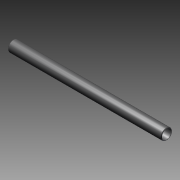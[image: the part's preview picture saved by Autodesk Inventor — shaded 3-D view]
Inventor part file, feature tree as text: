
AUTODESK INVENTOR PART (.ipt)
format: ipt  version: 2011 SP1 (Build 150282100, 282)  size: 112,128 bytes
history: native  units: in
note: dims shown in document units (in); Inventor stores cm internally (conversion verified against a paired STEP export)
features: other x42, revolve x1, sketch x1
ambient origin geometry x8: Origin, YZ Plane, XZ Plane, XY Plane, X Axis, Y Axis, Z Axis, Center Point
bodies: Solid1 (feature_tree)
feature tree (44):
  revolve  "Revolution1"  [1 undecoded]
  other  "cp1_XY"
  other  "cp1_YZ"
  other  "cp1_ZX"
  other  "cp1_X"
  other  "cp1_Y"
  other  "cp1_Z"
  other  "cp1_Center"
  other  "cp2_XY"
  other  "cp2_YZ"
  other  "cp2_ZX"
  other  "cp2_X"
  other  "cp2_Y"
  other  "cp2_Z"
  other  "cp2_Center"
  other  "cp3_XY"
  other  "cp3_YZ"
  other  "cp3_ZX"
  other  "cp3_X"
  other  "cp3_Y"
  other  "cp3_Z"
  other  "cp3_Center"
  other  "cp4_XY"
  other  "cp4_YZ"
  other  "cp4_ZX"
  other  "cp4_X"
  other  "cp4_Y"
  other  "cp4_Z"
  other  "cp4_Center"
  other  "tube_front_XY"
  other  "tube_front_YZ"
  other  "tube_front_ZX"
  other  "tube_front_X"
  other  "tube_front_Y"
  other  "tube_front_Z"
  other  "tube_front_Center"
  other  "tube_rear_XY"
  other  "tube_rear_YZ"
  other  "tube_rear_ZX"
  other  "tube_rear_X"
  other  "tube_rear_Y"
  other  "tube_rear_Z"
  other  "tube_rear_Center"
  sketch  "Sketch_1"  dims[d0=360.0deg]
note: 1 required parameter value undecoded (feature->parameter linkage not recoverable at this tier; creation-order binding heuristic only, values carry confidence <= 0.55)
